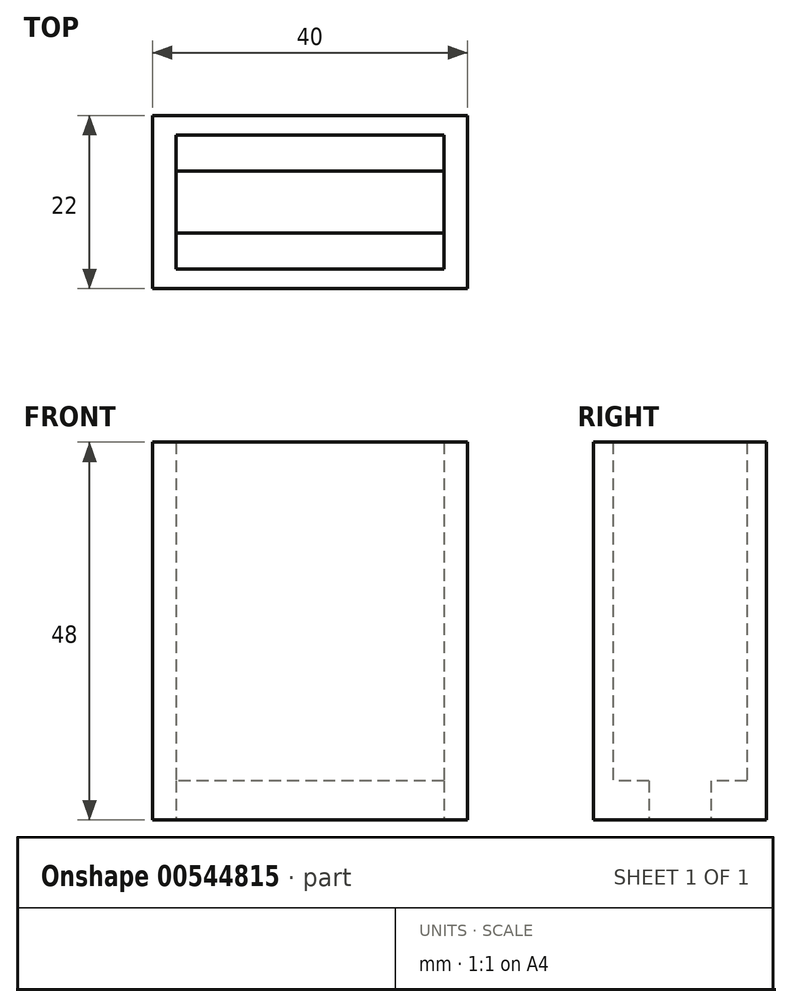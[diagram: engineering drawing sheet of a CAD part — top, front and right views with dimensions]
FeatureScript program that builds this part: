
annotation { "Feature Type Name" : "Feature", "Feature Type Description" : "" }
export const myFeature = defineFeature(function(context is Context, id is Id, definition is map)
    precondition{}
    {
        {
            var Q0;
            Q0=qCreatedBy(makeId("Top.planeOp"),FACE);
            var sketch = newSketch(context, id + "F0", { "sketchPlane" : qUnion([Q0])});
            skLineSegment(sketch, "E0.bottom", {"start": v(20, -11) * mm, "end": v(-20, -11) * mm});
            skLineSegment(sketch, "E0.top", {"start": v(20, 11) * mm, "end": v(-20, 11) * mm});
            skLineSegment(sketch, "E0.left", {"start": v(20, -11) * mm, "end": v(20, 11) * mm});
            skLineSegment(sketch, "E0.right", {"start": v(-20, -11) * mm, "end": v(-20, 11) * mm});
            skPoint(sketch, "E0.middle", {"position": v(0, 0) * mm});
            skLineSegment(sketch, "E1.bottom", {"start": v(17, -8.5) * mm, "end": v(-17, -8.5) * mm});
            skLineSegment(sketch, "E1.top", {"start": v(17, 8.5) * mm, "end": v(-17, 8.5) * mm});
            skLineSegment(sketch, "E1.left", {"start": v(17, -8.5) * mm, "end": v(17, 8.5) * mm});
            skLineSegment(sketch, "E1.right", {"start": v(-17, -8.5) * mm, "end": v(-17, 8.5) * mm});
            skLineSegment(sketch, "E2.bottom", {"start": v(17, -3.95) * mm, "end": v(-17, -3.95) * mm});
            skLineSegment(sketch, "E2.top", {"start": v(17, 3.95) * mm, "end": v(-17, 3.95) * mm});
            skLineSegment(sketch, "E2.left", {"start": v(17, -3.95) * mm, "end": v(17, 3.95) * mm});
            skLineSegment(sketch, "E2.right", {"start": v(-17, -3.95) * mm, "end": v(-17, 3.95) * mm});
            skSolve(sketch);
        }
        {
            var Q0;
            {var subQ0=sQuery(id+"F0.wireOp",EDGE,"E1.bottom");Q0=makeQuery(id+"F0.imprint","IMPRINT",FACE,{"disambiguationData":[TD([[makeQuery(id+"F0.imprint","IMPRINT",EDGE,{"derivedFrom":subQ0}),-1.0]])]});}
            var Q1;
            {var subQ0=sQuery(id+"F0.wireOp",EDGE,"E1.top");Q1=makeQuery(id+"F0.imprint","IMPRINT",FACE,{"disambiguationData":[TD([[makeQuery(id+"F0.imprint","IMPRINT",EDGE,{"derivedFrom":subQ0}),1.0]])]});}
            var Q2;
            Q2=makeQuery(id+"F0.imprint","IMPRINT",FACE,{"disambiguationData":[TD([[makeQuery(id+"F0.imprint","IMPRINT",EDGE,{"derivedFrom":sQuery(id+"F0.wireOp",EDGE,"E0.bottom")}),-1.0]])]});
            extrude(context, id + "F1", {"entities" : qUnion([Q0, Q1, Q2]), "depth" : 5 * mm, "offsetDistance" : 25 * mm});
        }
        {
            var Q0;
            Q0 = qSketchRegion(id + "F0", true);
            extrude(context, id + "F2", {"entities" : qUnion([Q0]), "operationType" : NewBodyOperationType.ADD, "depth" : 48 * mm, "offsetDistance" : 25 * mm});
        }
    });
